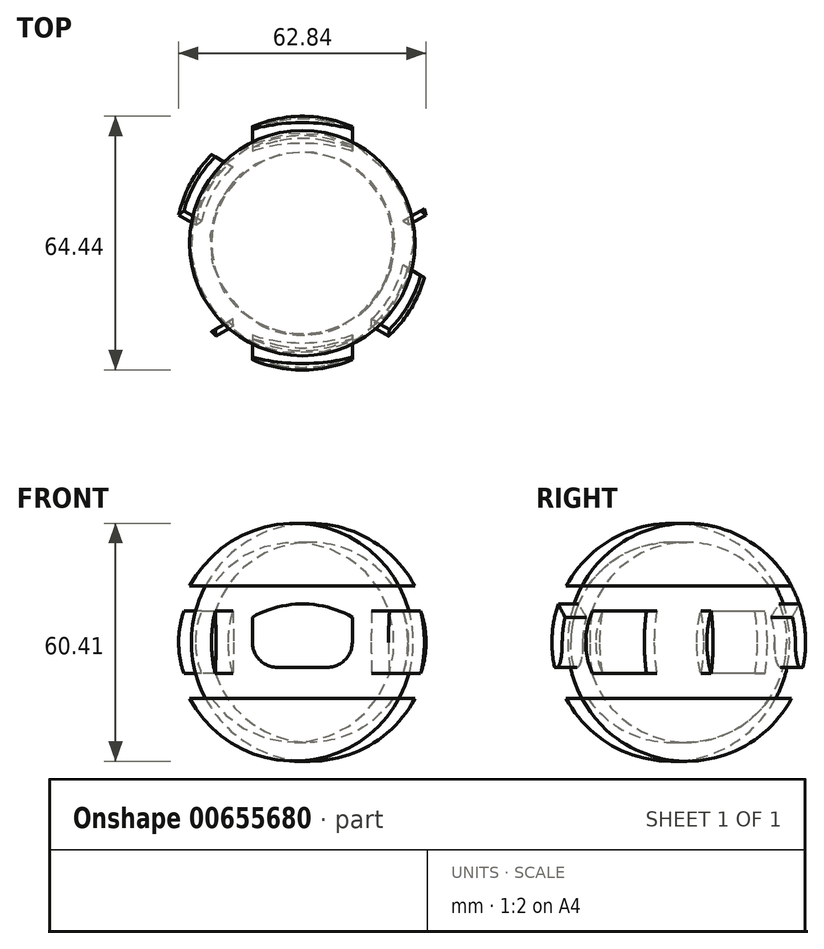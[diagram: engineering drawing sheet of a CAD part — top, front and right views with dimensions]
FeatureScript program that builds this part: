
annotation { "Feature Type Name" : "Feature", "Feature Type Description" : "" }
export const myFeature = defineFeature(function(context is Context, id is Id, definition is map)
    precondition{}
    {
        {
            var Q0;
            Q0=qCreatedBy(makeId("Top.planeOp"),FACE);
            var sketch = newSketch(context, id + "F0", { "sketchPlane" : qUnion([Q0])});
            skCircle(sketch, "E0", {"center": v(0, 0) * mm, "radius": 23.02 * mm});
            skSolve(sketch);
        }
        {
            var Q0;
            Q0=qCreatedBy(makeId("Front.planeOp"),FACE);
            var sketch = newSketch(context, id + "F1", { "sketchPlane" : qUnion([Q0])});
            skLineSegment(sketch, "E1", {"start": v(0, 0) * mm, "end": v(-23.02, 0) * mm});
            skLineSegment(sketch, "E2", {"start": v(-23.02, 0) * mm, "end": v(-23.02, 28.58) * mm});
            skLineSegment(sketch, "E3", {"start": v(-23.02, 28.58) * mm, "end": v(23.02, 28.58) * mm});
            skLineSegment(sketch, "E4", {"start": v(23.02, 28.58) * mm, "end": v(23.02, 0) * mm});
            skLineSegment(sketch, "E5", {"start": v(23.02, 0) * mm, "end": v(0, 0) * mm});
            skArc(sketch, "E6", {"start": v(23.02, 0) * mm, "mid": v(27.42, 14.29) * mm, "end": v(23.02, 28.58) * mm});
            skArc(sketch, "E7", {"start": v(28.63, 0) * mm, "mid": v(32.22, 14.29) * mm, "end": v(28.63, 28.58) * mm});
            skLineSegment(sketch, "E8", {"start": v(0, 0) * mm, "end": v(0, 28.58) * mm});
            skLineSegment(sketch, "E9", {"start": v(23.02, 28.58) * mm, "end": v(28.63, 28.58) * mm});
            skLineSegment(sketch, "E10", {"start": v(23.02, 0) * mm, "end": v(28.63, 0) * mm});
            skSolve(sketch);
        }
        {
            var Q0;
            Q0=makeQuery(id+"F1.imprint","IMPRINT",FACE,{"disambiguationData":[TD([[makeQuery(id+"F1.imprint","IMPRINT",EDGE,{"derivedFrom":sQuery(id+"F1.wireOp",EDGE,"E6")}),-1.0]])]});
            var Q1;
            Q1=sQuery(id+"F1.wireOp",EDGE,"E8");
            revolve(context, id + "F2", {"entities" : qUnion([Q0]), "axis" : qUnion([Q1]), "revolveType" : RevolveType.FULL});
        }
        {
            var Q0;
            Q0=qCreatedBy(makeId("Front.planeOp"),FACE);
            cPlane(context, id + "F3", {"entities" : qUnion([Q0]), "cplaneType" : CPlaneType.OFFSET, "offset" : 32.22 * mm, "width" : 152.4 * mm, "height" : 152.4 * mm});
        }
        {
            var Q0;
            Q0=qCreatedBy(id+"F3.planeOp",FACE);
            var sketch = newSketch(context, id + "F4", { "sketchPlane" : qUnion([Q0])});
            skLineSegment(sketch, "E11", {"start": v(0, 0) * mm, "end": v(0, 14.29) * mm});
            skLineSegment(sketch, "E12", {"start": v(0, 14.29) * mm, "end": v(0, 7.94) * mm});
            skLineSegment(sketch, "E13", {"start": v(0, 7.94) * mm, "end": v(6.35, 7.94) * mm});
            skLineSegment(sketch, "E14", {"start": v(12.7, 14.29) * mm, "end": v(12.7, 20.64) * mm});
            skLineSegment(sketch, "E15", {"start": v(12.7, 20.64) * mm, "end": v(-12.7, 20.64) * mm});
            skLineSegment(sketch, "E16", {"start": v(-12.7, 20.64) * mm, "end": v(-12.7, 14.29) * mm});
            skLineSegment(sketch, "E17", {"start": v(-6.35, 7.94) * mm, "end": v(0, 7.94) * mm});
            skPoint(sketch, "E18.visualSharp", {"position": v(12.7, 7.94) * mm});
            skArc(sketch, "E18.filletArc", {"start": v(6.35, 7.94) * mm, "mid": v(10.84, 9.8) * mm, "end": v(12.7, 14.29) * mm});
            skPoint(sketch, "E19.visualSharp", {"position": v(-12.7, 7.94) * mm});
            skArc(sketch, "E19.filletArc", {"start": v(-12.7, 14.29) * mm, "mid": v(-10.84, 9.8) * mm, "end": v(-6.35, 7.94) * mm});
            skArc(sketch, "E20", {"start": v(12.7, 20.64) * mm, "mid": v(0, 24.04) * mm, "end": v(-12.7, 20.64) * mm});
            skSolve(sketch);
        }
        {
            var Q0;
            Q0=makeQuery(id+"F4.imprint","IMPRINT",FACE,{"disambiguationData":[TD([[makeQuery(id+"F4.imprint","IMPRINT",EDGE,{"derivedFrom":sQuery(id+"F4.wireOp",EDGE,"E13")}),1.0]])]});
            var Q1;
            Q1=makeQuery(id+"F4.imprint","IMPRINT",FACE,{"disambiguationData":[TD([[makeQuery(id+"F4.imprint","IMPRINT",EDGE,{"derivedFrom":sQuery(id+"F4.wireOp",EDGE,"E15")}),-1.0]])]});
            var Q2;
            {var subQ0=sQuery(id+"F4.wireOp",EDGE,"E13");Q2=makeQuery(id+"F4.imprint","IMPRINT",FACE,{"disambiguationData":[TD([[makeQuery(id+"F4.imprint","IMPRINT",EDGE,{"derivedFrom":subQ0}),-1.0]])]});}
            var Q3;
            {var subQ0=sQuery(id+"F4.wireOp",EDGE,"E17");Q3=makeQuery(id+"F4.imprint","IMPRINT",FACE,{"disambiguationData":[TD([[makeQuery(id+"F4.imprint","IMPRINT",EDGE,{"derivedFrom":subQ0}),-1.0]])]});}
            extrude(context, id + "F5", {"entities" : qUnion([Q0, Q1, Q2, Q3]), "operationType" : NewBodyOperationType.REMOVE, "endBound" : BoundingType.THROUGH_ALL, "oppositeDirection" : true, "depth" : 25.4 * mm, "offsetDistance" : 25.4 * mm});
        }
        {
            var Q0;
            Q0=qCreatedBy(makeId("Front.planeOp"),FACE);
            var Q1;
            Q1=makeQuery(id+"F2.opRevolve","SWEPT_EDGE",EDGE,{"disambiguationData":[OSD([sQuery(id+"F1.wireOp",EDGE,"E3"),sQuery(id+"F1.wireOp",EDGE,"E4"),sQuery(id+"F1.wireOp",EDGE,"E6"),sQuery(id+"F1.wireOp",EDGE,"E9")])]});
            cPlane(context, id + "F6", {"entities" : qUnion([Q0, Q1]), "cplaneType" : CPlaneType.LINE_ANGLE, "offset" : 25.4 * mm, "angle" : 60 * degree, "width" : 152.4 * mm, "height" : 152.4 * mm});
        }
        {
            var Q0;
            Q0=qCreatedBy(id+"F6.planeOp",FACE);
            cPlane(context, id + "F7", {"entities" : qUnion([Q0]), "cplaneType" : CPlaneType.OFFSET, "offset" : 32.22 * mm, "oppositeDirection" : true, "width" : 152.4 * mm, "height" : 152.4 * mm});
        }
        {
            var Q0;
            Q0=qCreatedBy(id+"F7.planeOp",FACE);
            var sketch = newSketch(context, id + "F8", { "sketchPlane" : qUnion([Q0])});
            skLineSegment(sketch, "E21", {"start": v(0, 0) * mm, "end": v(0, 14.29) * mm});
            skLineSegment(sketch, "E22", {"start": v(0, 14.29) * mm, "end": v(0, 22.23) * mm});
            skLineSegment(sketch, "E23", {"start": v(0, 22.23) * mm, "end": v(0, 6.35) * mm});
            skLineSegment(sketch, "E24", {"start": v(7.94, 1.59) * mm, "end": v(7.94, 6.35) * mm});
            skLineSegment(sketch, "E25", {"start": v(7.94, 6.35) * mm, "end": v(7.94, 14.29) * mm});
            skLineSegment(sketch, "E26", {"start": v(7.94, 14.29) * mm, "end": v(7.94, 22.23) * mm});
            skLineSegment(sketch, "E27", {"start": v(7.94, 6.35) * mm, "end": v(-7.94, 6.35) * mm});
            skLineSegment(sketch, "E28", {"start": v(-7.94, 6.35) * mm, "end": v(-7.94, 22.23) * mm});
            skLineSegment(sketch, "E29", {"start": v(-7.94, 22.23) * mm, "end": v(7.94, 22.23) * mm});
            skLineSegment(sketch, "E30", {"start": v(7.94, 22.23) * mm, "end": v(7.94, 6.35) * mm});
            skLineSegment(sketch, "E31", {"start": v(7.94, 6.35) * mm, "end": v(7.94, 6.35) * mm});
            skArc(sketch, "E32", {"start": v(7.94, 6.35) * mm, "mid": v(9.52, 14.29) * mm, "end": v(7.94, 22.23) * mm});
            skArc(sketch, "E33.MirrorCS", {"start": v(-7.94, 6.35) * mm, "mid": v(-9.52, 14.29) * mm, "end": v(-7.94, 22.23) * mm});
            skSolve(sketch);
        }
        {
            var Q0;
            Q0=makeQuery(id+"F8.imprint","IMPRINT",FACE,{"disambiguationData":[TD([[makeQuery(id+"F8.imprint","IMPRINT",EDGE,{"derivedFrom":sQuery(id+"F8.wireOp",EDGE,"E30")}),1.0]])]});
            var Q1;
            {var subQ0=sQuery(id+"F8.wireOp",EDGE,"E23");Q1=makeQuery(id+"F8.imprint","IMPRINT",FACE,{"disambiguationData":[TD([[makeQuery(id+"F8.imprint","IMPRINT",EDGE,{"derivedFrom":subQ0}),1.0]])]});}
            var Q2;
            {var subQ0=sQuery(id+"F8.wireOp",EDGE,"E23");Q2=makeQuery(id+"F8.imprint","IMPRINT",FACE,{"disambiguationData":[TD([[makeQuery(id+"F8.imprint","IMPRINT",EDGE,{"derivedFrom":subQ0}),-1.0]])]});}
            var Q3;
            Q3=makeQuery(id+"F8.imprint","IMPRINT",FACE,{"disambiguationData":[TD([[makeQuery(id+"F8.imprint","IMPRINT",EDGE,{"derivedFrom":sQuery(id+"F8.wireOp",EDGE,"E28")}),1.0]])]});
            extrude(context, id + "F9", {"entities" : qUnion([Q0, Q1, Q2, Q3]), "operationType" : NewBodyOperationType.REMOVE, "endBound" : BoundingType.THROUGH_ALL, "depth" : 25.4 * mm, "offsetDistance" : 25.4 * mm});
        }
        {
            var Q0;
            Q0=qCreatedBy(makeId("Front.planeOp"),FACE);
            var Q1;
            Q1=makeQuery(id+"F2.opRevolve","SWEPT_EDGE",EDGE,{"disambiguationData":[OSD([sQuery(id+"F1.wireOp",EDGE,"E3"),sQuery(id+"F1.wireOp",EDGE,"E4"),sQuery(id+"F1.wireOp",EDGE,"E6"),sQuery(id+"F1.wireOp",EDGE,"E9")])]});
            cPlane(context, id + "F10", {"entities" : qUnion([Q0, Q1]), "cplaneType" : CPlaneType.LINE_ANGLE, "offset" : 25.4 * mm, "angle" : 60 * degree, "oppositeDirection" : true, "width" : 152.4 * mm, "height" : 152.4 * mm});
        }
        {
            var Q0;
            Q0=qCreatedBy(id+"F10.planeOp",FACE);
            cPlane(context, id + "F11", {"entities" : qUnion([Q0]), "cplaneType" : CPlaneType.OFFSET, "offset" : 50.8 * mm, "width" : 152.4 * mm, "height" : 152.4 * mm});
        }
        {
            var Q0;
            Q0=qCreatedBy(id+"F11.planeOp",FACE);
            var sketch = newSketch(context, id + "F12", { "sketchPlane" : qUnion([Q0])});
            skLineSegment(sketch, "E34", {"start": v(-7.94, 14.29) * mm, "end": v(-7.94, 22.22) * mm});
            skLineSegment(sketch, "E35", {"start": v(-7.94, 22.22) * mm, "end": v(-7.94, 6.35) * mm});
            skLineSegment(sketch, "E36", {"start": v(0, 0) * mm, "end": v(0, 0) * mm});
            skLineSegment(sketch, "E37", {"start": v(0, 0) * mm, "end": v(0, 6.35) * mm});
            skLineSegment(sketch, "E38", {"start": v(0, 6.35) * mm, "end": v(0, 14.29) * mm});
            skLineSegment(sketch, "E39", {"start": v(0, 14.29) * mm, "end": v(0, 22.23) * mm});
            skLineSegment(sketch, "E40", {"start": v(0, 6.35) * mm, "end": v(-7.94, 6.35) * mm});
            skLineSegment(sketch, "E41", {"start": v(-7.94, 6.35) * mm, "end": v(-7.94, 22.23) * mm});
            skLineSegment(sketch, "E42", {"start": v(-7.94, 22.23) * mm, "end": v(7.94, 22.23) * mm});
            skLineSegment(sketch, "E43", {"start": v(7.94, 22.23) * mm, "end": v(7.94, 6.35) * mm});
            skLineSegment(sketch, "E44", {"start": v(7.94, 6.35) * mm, "end": v(0, 6.35) * mm});
            skArc(sketch, "E45", {"start": v(7.94, 6.35) * mm, "mid": v(9.52, 14.29) * mm, "end": v(7.94, 22.23) * mm});
            skArc(sketch, "E46.MirrorCS", {"start": v(-7.94, 6.35) * mm, "mid": v(-9.52, 14.29) * mm, "end": v(-7.94, 22.23) * mm});
            skSolve(sketch);
        }
        {
            var Q0;
            {var subQ0=sQuery(id+"F12.wireOp",EDGE,"E46.MirrorCS");Q0=makeQuery(id+"F12.imprint","IMPRINT",FACE,{"disambiguationData":[TD([[makeQuery(id+"F12.imprint","IMPRINT",EDGE,{"derivedFrom":subQ0}),-1.0]])]});}
            var Q1;
            Q1=makeQuery(id+"F12.imprint","IMPRINT",FACE,{"disambiguationData":[TD([[makeQuery(id+"F12.imprint","IMPRINT",EDGE,{"derivedFrom":sQuery(id+"F12.wireOp",EDGE,"E38")}),1.0]])]});
            var Q2;
            Q2=makeQuery(id+"F12.imprint","IMPRINT",FACE,{"disambiguationData":[TD([[makeQuery(id+"F12.imprint","IMPRINT",EDGE,{"derivedFrom":sQuery(id+"F12.wireOp",EDGE,"E38")}),-1.0]])]});
            var Q3;
            Q3=makeQuery(id+"F12.imprint","IMPRINT",FACE,{"disambiguationData":[TD([[makeQuery(id+"F12.imprint","IMPRINT",EDGE,{"derivedFrom":sQuery(id+"F12.wireOp",EDGE,"E43")}),1.0]])]});
            extrude(context, id + "F13", {"entities" : qUnion([Q0, Q1, Q2, Q3]), "operationType" : NewBodyOperationType.REMOVE, "endBound" : BoundingType.THROUGH_ALL, "oppositeDirection" : true, "depth" : 25.4 * mm, "offsetDistance" : 25.4 * mm});
        }
    });
